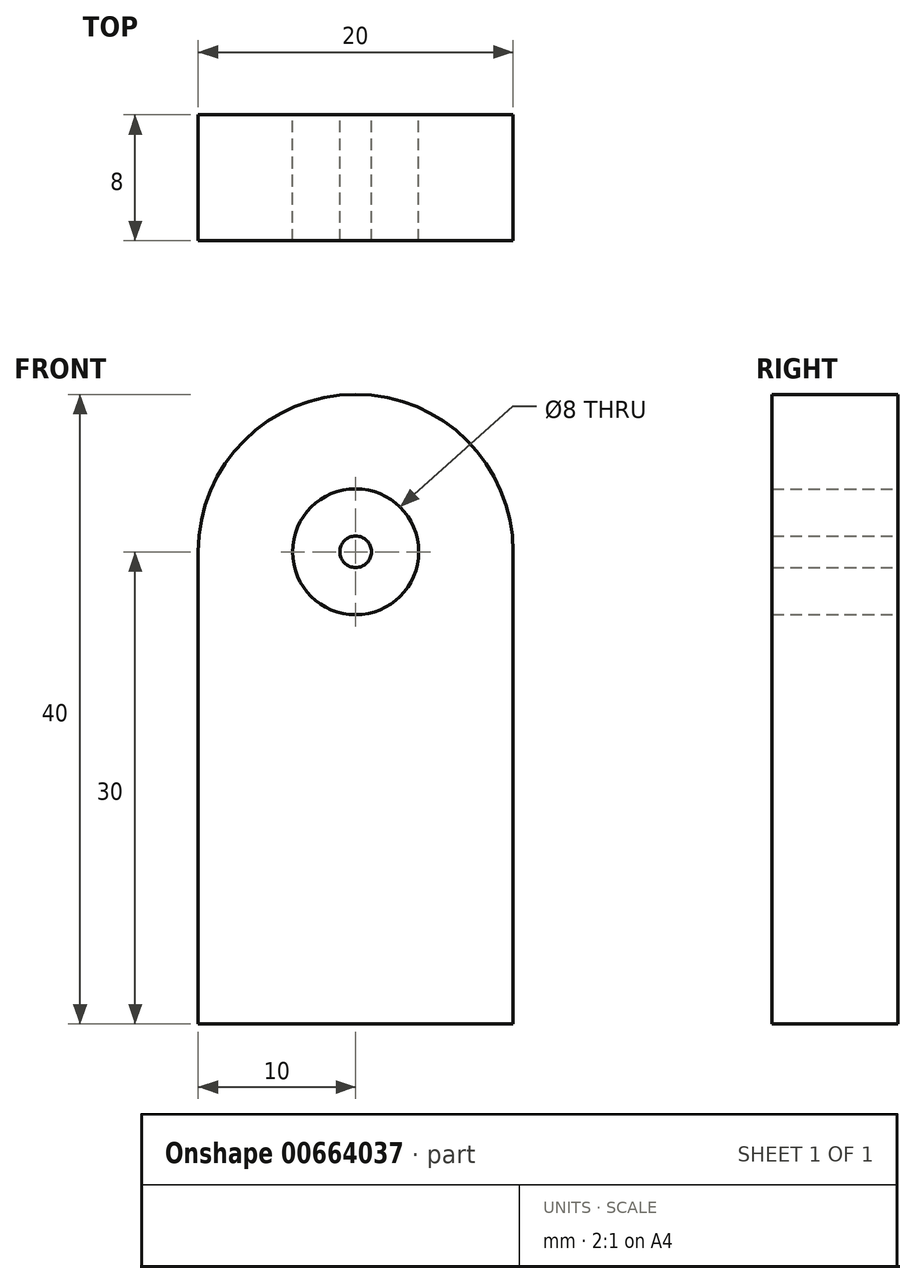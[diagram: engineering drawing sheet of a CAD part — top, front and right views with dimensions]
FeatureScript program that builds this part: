
annotation { "Feature Type Name" : "Feature", "Feature Type Description" : "" }
export const myFeature = defineFeature(function(context is Context, id is Id, definition is map)
    precondition{}
    {
        {
            var Q0;
            Q0=qCreatedBy(makeId("Front.planeOp"),FACE);
            var sketch = newSketch(context, id + "F0", { "sketchPlane" : qUnion([Q0])});
            skCircle(sketch, "E0", {"center": v(0, 30) * mm, "radius": 4 * mm});
            skArc(sketch, "E1", {"start": v(10, 30) * mm, "mid": v(0, 40) * mm, "end": v(-10, 30) * mm});
            skLineSegment(sketch, "E2", {"start": v(-10, 30) * mm, "end": v(-10, 0) * mm});
            skLineSegment(sketch, "E3", {"start": v(-10, 0) * mm, "end": v(10, 0) * mm});
            skLineSegment(sketch, "E4", {"start": v(10, 0) * mm, "end": v(10, 30) * mm});
            skSolve(sketch);
        }
        {
            var Q0;
            Q0 = qSketchRegion(id + "F0", true);
            extrude(context, id + "F1", {"entities" : qUnion([Q0]), "depth" : 8 * mm, "offsetDistance" : 25 * mm});
        }
        {
            var Q0;
            Q0=qCreatedBy(makeId("Front.planeOp"),FACE);
            var sketch = newSketch(context, id + "F2", { "sketchPlane" : qUnion([Q0])});
            skCircle(sketch, "E5", {"center": v(0, 30) * mm, "radius": 1 * mm});
            skSolve(sketch);
        }
        {
            var Q0;
            Q0 = qSketchRegion(id + "F2", true);
            extrude(context, id + "F3", {"entities" : qUnion([Q0]), "depth" : 8 * mm, "offsetDistance" : 25 * mm});
        }
    });
